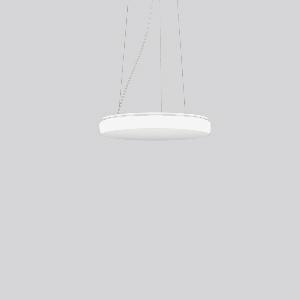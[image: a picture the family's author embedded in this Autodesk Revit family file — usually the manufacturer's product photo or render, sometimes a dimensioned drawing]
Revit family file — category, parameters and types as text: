
# Revit family: flat_polymero_kreis_slim_312241_002_3_76_6ecc
name_source: partatom
category: Lighting Fixtures
units: mm (PartAtom-declared; Revit-internal decimal feet)

## family parameters
Cut with Voids When Loaded = No
Host = Face
Light Source = No
Part Type = Normal
Room Calculation Point = No
Round Connector Dimension = Use Diameter
Shared = No

## types (1)
- FLAT POLYMERO KREIS SLIM (1 x LED Modul 840, 3150 lm, 4000)
    Apparent Load = 31 VA
    CIE Flux Codes = 41 72 91 83 100
    Color Rendering = 80
    Color Temperature = 4000
    Default Elevation = 1800 mm
    Description = Series: FLAT POLYMERO KREIS SLIM
Decorative round LED pendant luminaire. Base and canopy: metal, powder-coated, white. Canopy Ø 205 mm, h 35 mm. Diffuser made of non-yellowing plastic (PMMA), opal. Diffuser fastening: patented push system. Homogeneous and smooth light distribution. Suitable for pendant. 3-point steel cable suspension, steplessly adjustable. Special lengths available on request. TouchDim sensor capable. Light and/or presence sensors can be integrated. 
Colour: white
Diameter: 460 mm
Height: 68 mm
Suspension length: 200-1300 mm
Lamp: LED exchangeable
Socket: without socket
Colour temperature: 4000K
Colour rendering index (CRI): 83
System power: 31 W
Rated luminous flux: 3150 lm
Luminous efficiency: 102 lm/W
Control gear: AC power, DALI dimmable
Protection class: I
Type of protection: IP 40
    Height = 68 mm
    Lamp = 1 x LED Modul 840
    Lamp Light Flux = 3150 lm
    Lamp count = 1
    Length = 460 mm
    Lifetime = 50000 h
    Luminous efficacy = 102 lm/W
    Manufacturer = RZB
    ModVariant = No
    Model = 312241.002.3.76
    Mounting Place = Ceiling
    Mounting Type = Pendant
    Number of Poles = 1
    OnlyDefault = Yes
    Power Factor = 1
    Product Name = FLAT POLYMERO KREIS SLIM
    Product group = Pendant luminaires
    ProductGroupID = 902
    Protection Class = Protection class I
    Protection Degree = IP 40
    RLX_Detail_Level = 1
    RLX_Emergency_Light_Flux = 0 lm
    RLX_Emergency_Type = 0
    RLX_Emergency_Type_DB = No
    RlxData = <blob elided: 57389 chars, md5=cfb1db42>
    Socket = socket
    Standby Power = 0 W
    System Light Flux = 3150 lm
    System Power = 31 W
    Type Comments = Product without accessories
    Type Image = 312090.002.jpg
    URL = http://relux.com
    VarID = ---
    Voltage = 230 V
    Voltage Range = 220-240 V
    Weight = 0.00 kg
    Width = 0 mm  [stored 0 ft]

note: [stored X ft] marks values corroborated as IEEE doubles in the binary element streams (Revit-internal decimal feet)

## geometry (parser evidence)
native form markers: Blend x4, Sweep x13
no freeform markers — native parametric forms only
